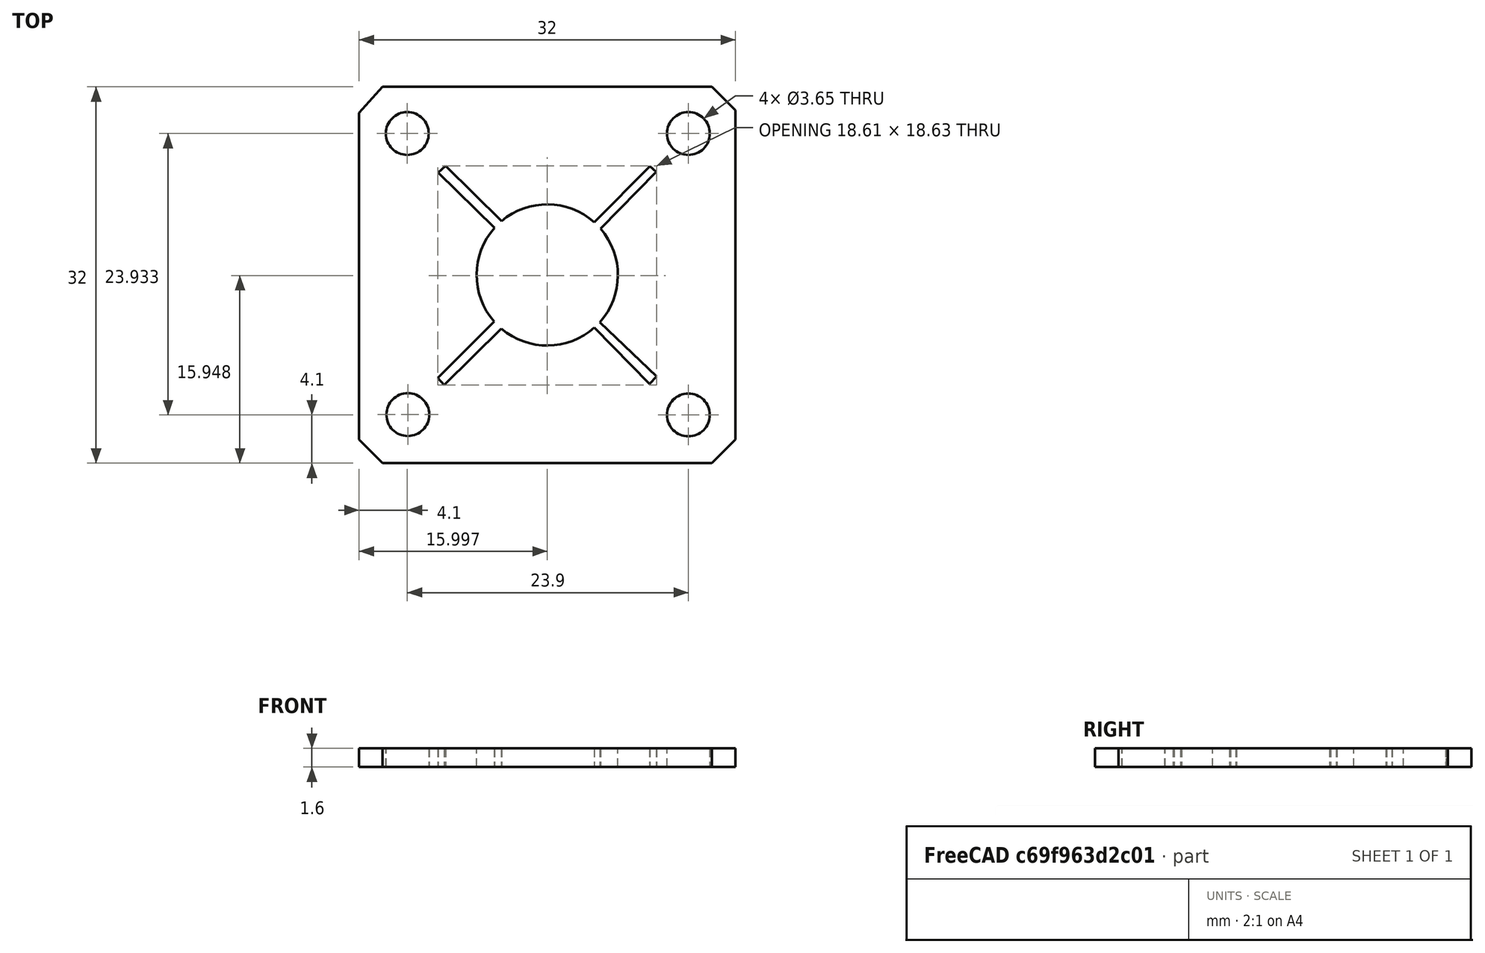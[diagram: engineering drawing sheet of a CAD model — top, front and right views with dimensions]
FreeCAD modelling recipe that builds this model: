
FCSTD DOCUMENT  (FreeCAD 0.18R16146 (Git))
Label: FSR
License: All rights reserved
LicenseURL: http://en.wikipedia.org/wiki/All_rights_reserved
objects: Image::ImagePlane×5, Sketcher::SketchObject×1, PartDesign::Pad×1, PartDesign::Body×1
note: 4 computed .brp shape members not serialized (recipe doc carries the construction recipe); baked Part::Feature solids carry a one-line shape summary decoded from their .brp

FEATURE [Image::ImagePlane] ImagePlane
  XSize = 32
  YSize = 32
FEATURE [Sketcher::SketchObject] Sketch
  MapMode = 5
  Support = -> [XY_Plane]
  sketch-geometry (28):
    g0: ArcOfCircle CenterX=0 CenterY=0 CenterZ=0 NormalX=0 NormalY=0 NormalZ=1 AngleXU=0 Radius=6.00469 StartAngle=0.845222 EndAngle=2.27546
    g1: LineSegment StartX=-8.65424 StartY=9.26405 StartZ=0 EndX=-9.26071 EndY=8.72027 EndZ=0
    g2: LineSegment StartX=-9.26071 StartY=8.72027 StartZ=0 EndX=-4.46624 EndY=4.01361 EndZ=0
    g3: LineSegment StartX=-3.88972 StartY=4.57454 StartZ=0 EndX=-8.65424 EndY=9.26405 EndZ=0
    g4: LineSegment StartX=3.9845 StartY=4.49222 StartZ=0 EndX=8.72725 EndY=9.24452 EndZ=0
    g5: LineSegment StartX=8.72725 StartY=9.24452 StartZ=0 EndX=9.27408 EndY=8.77581 EndZ=0
    g6: LineSegment StartX=9.27408 StartY=8.77581 StartZ=0 EndX=4.53655 EndY=3.93396 EndZ=0
    g7: LineSegment StartX=4.46051 StartY=-4.01997 StartZ=0 EndX=9.30265 EndY=-8.63837 EndZ=0
    g8: LineSegment StartX=9.30265 StartY=-8.63837 StartZ=0 EndX=8.69723 EndY=-9.27113 EndZ=0
    g9: LineSegment StartX=8.69723 StartY=-9.27113 StartZ=0 EndX=4.00289 EndY=-4.47584 EndZ=0
    g10: LineSegment StartX=-9.30921 StartY=-8.74383 StartZ=0 EndX=-4.50486 EndY=-3.97021 EndZ=0
    g11: LineSegment StartX=-3.90165 StartY=-4.56436 StartZ=0 EndX=-8.76237 EndY=-9.36878 EndZ=0
    g12: LineSegment StartX=-8.76237 StartY=-9.36878 StartZ=0 EndX=-9.30921 EndY=-8.74383 EndZ=0
    g13: LineSegment StartX=14 StartY=16 StartZ=0 EndX=16 EndY=14 EndZ=0
    g14: LineSegment StartX=16 StartY=14 StartZ=0 EndX=16 EndY=-14 EndZ=0
    g15: LineSegment StartX=16 StartY=-14 StartZ=0 EndX=14 EndY=-16 EndZ=0
    g16: LineSegment StartX=14 StartY=-16 StartZ=0 EndX=-14 EndY=-16 EndZ=0
    g17: LineSegment StartX=-14 StartY=-16 StartZ=0 EndX=-16 EndY=-14 EndZ=0
    g18: LineSegment StartX=-16 StartY=-14 StartZ=0 EndX=-16 EndY=13.7962 EndZ=0
    g19: LineSegment StartX=-16 StartY=13.7962 StartZ=0 EndX=-14 EndY=16 EndZ=0
    g20: LineSegment StartX=-14 StartY=16 StartZ=0 EndX=14 EndY=16 EndZ=0
    g21: Circle CenterX=-11.9 CenterY=12.0325 CenterZ=0 NormalX=0 NormalY=0 NormalZ=1 AngleXU=0 Radius=1.82287
    g22: Circle CenterX=12 CenterY=12.0325 CenterZ=0 NormalX=0 NormalY=0 NormalZ=1 AngleXU=0 Radius=1.82287
    g23: Circle CenterX=-11.8523 CenterY=-11.8729 CenterZ=0 NormalX=0 NormalY=0 NormalZ=1 AngleXU=0 Radius=1.82287
    g24: Circle CenterX=12 CenterY=-11.9 CenterZ=0 NormalX=0 NormalY=0 NormalZ=1 AngleXU=0 Radius=1.82287
    g25: ArcOfCircle CenterX=0 CenterY=0 CenterZ=0 NormalX=0 NormalY=0 NormalZ=1 AngleXU=0 Radius=6.00469 StartAngle=2.40952 EndAngle=3.86399
    g26: ArcOfCircle CenterX=0 CenterY=0 CenterZ=0 NormalX=0 NormalY=0 NormalZ=1 AngleXU=0 Radius=6.00469 StartAngle=4.00511 EndAngle=5.44206
    g27: ArcOfCircle CenterX=0 CenterY=0 CenterZ=0 NormalX=0 NormalY=0 NormalZ=1 AngleXU=0 Radius=6.00469 StartAngle=5.54969 EndAngle=6.99756
  constraints (30):
    c: Coincident(g1,g2)
    c: Coincident(g3,g1)
    c: Coincident(g4,g5)
    c: Coincident(g5,g6)
    c: Coincident(g7,g8)
    c: Coincident(g8,g9)
    c: Coincident(g11,g12)
    c: Coincident(g12,g10)
    c: Coincident(g13,g14)
    c: Coincident(g14,g15)
    c: Coincident(g15,g16)
    c: Coincident(g16,g17)
    c: Coincident(g17,g18)
    c: Coincident(g18,g19)
    c: Coincident(g19,g20)
    c: Coincident(g20,g13)
    c: Coincident(g4,g0)
    c: Coincident(g6,g27)
    c: Equal(g0,g25)
    c: Coincident(g0,g3)
    c: Coincident(g0,g25)
    c: Coincident(g2,g25)
    c: Equal(g25,g26)
    c: Coincident(g25,g10)
    c: Coincident(g25,g26)
    c: Coincident(g11,g26)
    c: Equal(g26,g27)
    c: Coincident(g26,g9)
    c: Coincident(g26,g27)
    c: Coincident(g7,g27)
FEATURE [PartDesign::Pad] Pad
  Length = 1.6
  Length2 = 100
  Profile = -> Sketch
  Reversed = true
  Type = 0
FEATURE [PartDesign::Body] Body
  Group = -> [Sketch,Pad]
  Origin = -> Origin
  Tip = -> Pad
FEATURE [Image::ImagePlane] ImagePlane001
  Placement = pos=(12.1629,-0.849208,9.58013) rot=(-0.106596,0.257344,0.960422;3.89884rad)
  XSize = 8
  YSize = 39
FEATURE [Image::ImagePlane] ImagePlane002
  Placement = pos=(-0.673792,-12.6946,9.47391) rot=(-0.106596,-0.257344,-0.960422;3.89884rad)
  XSize = 8
  YSize = 39
FEATURE [Image::ImagePlane] ImagePlane003
  Placement = pos=(-12.1767,0.86303,9.51295) rot=(-0.529904,-0.219493,-0.819161;5.34686rad)
  XSize = 8
  YSize = 39
FEATURE [Image::ImagePlane] ImagePlane004
  Placement = pos=(3.15474,12.9128,9.53083) rot=(-0.529904,0.219493,0.819161;5.34686rad)
  XSize = 8
  YSize = 39
